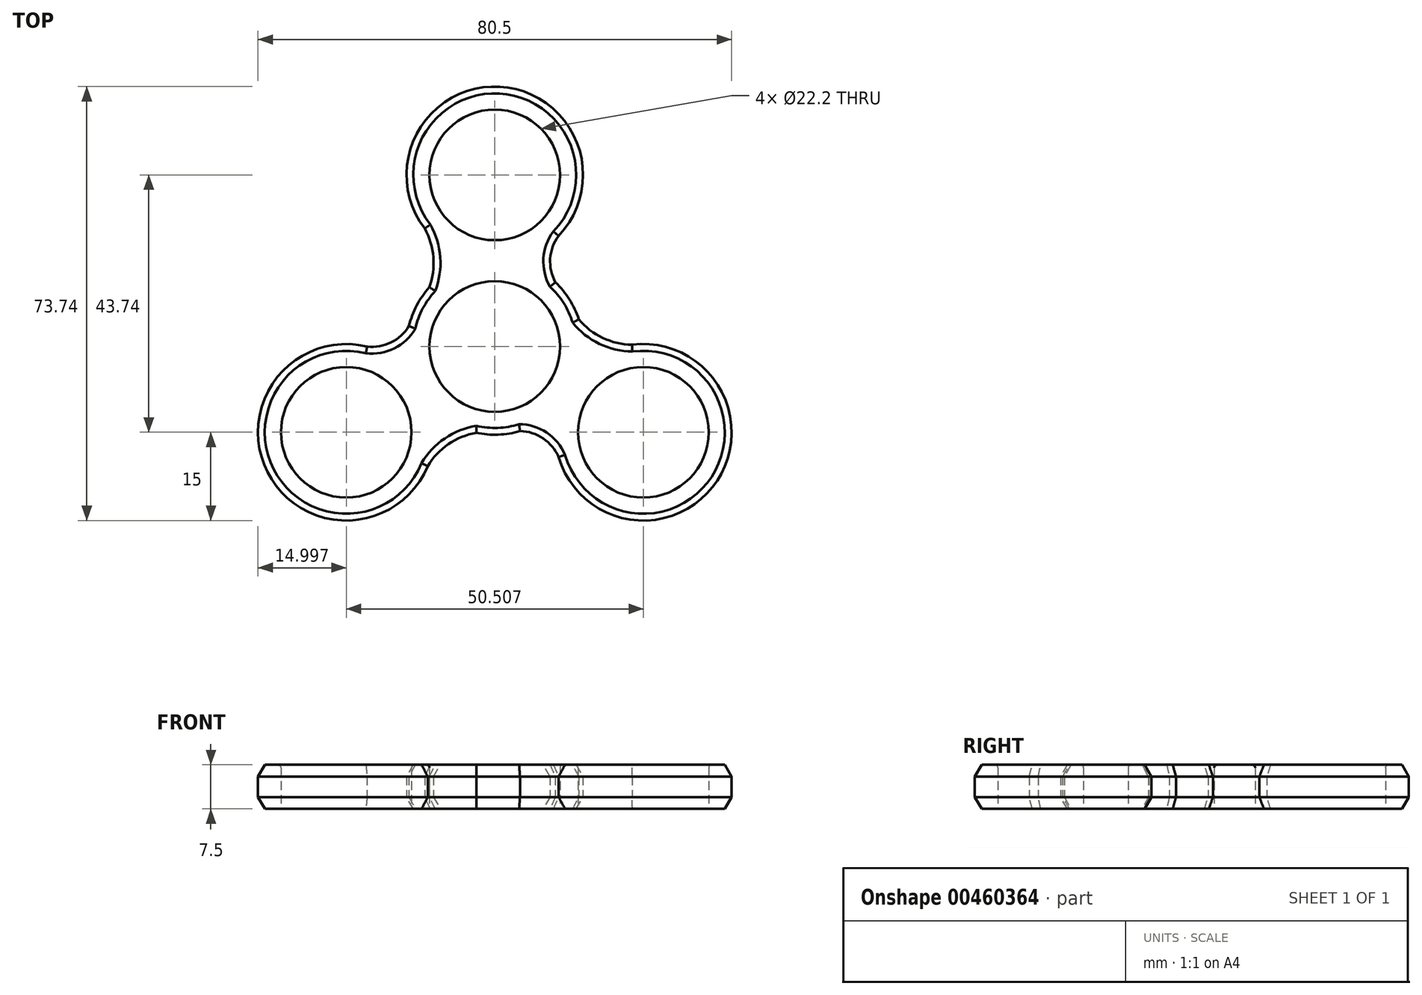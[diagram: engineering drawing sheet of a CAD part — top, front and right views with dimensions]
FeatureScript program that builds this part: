
annotation { "Feature Type Name" : "Feature", "Feature Type Description" : "" }
export const myFeature = defineFeature(function(context is Context, id is Id, definition is map)
    precondition{}
    {
        {
            var Q0;
            Q0=qCreatedBy(makeId("Top.planeOp"),FACE);
            var sketch = newSketch(context, id + "F0", { "sketchPlane" : qUnion([Q0])});
            skCircle(sketch, "E0", {"center": v(0, 0) * mm, "radius": 11.1 * mm});
            skCircle(sketch, "E1", {"center": v(0, 0) * mm, "radius": 15 * mm});
            skCircle(sketch, "E2", {"center": v(0, 29.16) * mm, "radius": 11.1 * mm});
            skCircle(sketch, "E3", {"center": v(0, 29.16) * mm, "radius": 15 * mm});
            skArc(sketch, "E4", {"start": v(-11.13, 10.06) * mm, "mid": v(-10.43, 15.14) * mm, "end": v(-11.92, 20.05) * mm});
            skArc(sketch, "E5", {"start": v(10.85, 18.8) * mm, "mid": v(9.41, 14.93) * mm, "end": v(10.3, 10.9) * mm});
            skCircle(sketch, "E6.1.0", {"center": v(-25.25, -14.58) * mm, "radius": 15 * mm});
            skCircle(sketch, "E6.1.1", {"center": v(-25.25, -14.58) * mm, "radius": 11.1 * mm});
            skArc(sketch, "E6.1.2", {"start": v(-3.15, -14.67) * mm, "mid": v(-7.9, -16.6) * mm, "end": v(-11.4, -20.35) * mm});
            skArc(sketch, "E6.1.3", {"start": v(-21.7, 0) * mm, "mid": v(-17.64, 0.69) * mm, "end": v(-14.6, 3.47) * mm});
            skCircle(sketch, "E6.2.0", {"center": v(25.25, -14.58) * mm, "radius": 15 * mm});
            skCircle(sketch, "E6.2.1", {"center": v(25.25, -14.58) * mm, "radius": 11.1 * mm});
            skArc(sketch, "E6.2.2", {"start": v(14.27, 4.6) * mm, "mid": v(18.33, 1.47) * mm, "end": v(23.33, 0.3) * mm});
            skArc(sketch, "E6.2.3", {"start": v(10.86, -18.8) * mm, "mid": v(8.22, -15.62) * mm, "end": v(4.29, -14.37) * mm});
            skSolve(sketch);
        }
        {
            var Q0;
            Q0=qSketchRegion(id+"F0",true);
            extrude(context, id + "F1", {"entities" : qUnion([Q0]), "depth" : 7.5 * mm, "offsetDistance" : 25 * mm});
        }
        {
            var Q0;
            {var subQ0=sQuery(id+"F0.wireOp",EDGE,"E6.2.0");var subQ1=sQuery(id+"F0.wireOp",EDGE,"E1");var subQ2=makeQuery(id+"F0.imprint","INTERSECT",VERTEX,{"disambiguationData":[OD(0.0)],"derivedFrom":[subQ1,subQ0]});Q0=makeQuery(id+"F0.imprint","IMPRINT",FACE,{"disambiguationData":[TD([[makeQuery(id+"F0.imprint","IMPRINT",EDGE,{"disambiguationData":[TD([[subQ2,-1.0]])],"derivedFrom":subQ1}),1.0]])]});}
            var Q1;
            {var subQ0=sQuery(id+"F0.wireOp",EDGE,"E6.1.0");var subQ1=sQuery(id+"F0.wireOp",EDGE,"E1");var subQ2=makeQuery(id+"F0.imprint","INTERSECT",VERTEX,{"disambiguationData":[OD(0.0)],"derivedFrom":[subQ1,subQ0]});Q1=makeQuery(id+"F0.imprint","IMPRINT",FACE,{"disambiguationData":[TD([[makeQuery(id+"F0.imprint","IMPRINT",EDGE,{"disambiguationData":[TD([[subQ2,-1.0]])],"derivedFrom":subQ1}),1.0]])]});}
            var Q2;
            {var subQ0=sQuery(id+"F0.wireOp",EDGE,"E3");var subQ1=sQuery(id+"F0.wireOp",EDGE,"E1");var subQ2=makeQuery(id+"F0.imprint","INTERSECT",VERTEX,{"disambiguationData":[OD(0.0)],"derivedFrom":[subQ1,subQ0]});Q2=makeQuery(id+"F0.imprint","IMPRINT",FACE,{"disambiguationData":[TD([[makeQuery(id+"F0.imprint","IMPRINT",EDGE,{"disambiguationData":[TD([[subQ2,-1.0]])],"derivedFrom":subQ1}),1.0]])]});}
            extrude(context, id + "F2", {"entities" : qUnion([Q0, Q1, Q2]), "operationType" : NewBodyOperationType.ADD, "depth" : 7.5 * mm, "offsetDistance" : 25 * mm});
        }
        {
            var Q0;
            Q0=makeQuery(id+"F1.opExtrude","CAP_EDGE",EDGE,{"disambiguationData":[OSD([sQuery(id+"F0.wireOp",EDGE,"E2")])],"isStart":false});
            var Q1;
            Q1=makeQuery(id+"F1.opExtrude","CAP_EDGE",EDGE,{"disambiguationData":[OSD([sQuery(id+"F0.wireOp",EDGE,"E0")])],"isStart":false});
            var Q2;
            Q2=makeQuery(id+"F1.opExtrude","CAP_EDGE",EDGE,{"disambiguationData":[OSD([sQuery(id+"F0.wireOp",EDGE,"E6.2.1")])],"isStart":false});
            var Q3;
            Q3=makeQuery(id+"F1.opExtrude","CAP_EDGE",EDGE,{"disambiguationData":[OSD([sQuery(id+"F0.wireOp",EDGE,"E6.1.1")])],"isStart":false});
            fillet(context, id + "F3", {"entities" : qUnion([Q0, Q1, Q2, Q3]), "radius" : 0.5 * mm, "tangentPropagation" : true, "allowEdgeOverflow" : false});
        }
        {
            var Q0;
            {var subQ0=sQuery(id+"F0.wireOp",EDGE,"E6.1.0");Q0=makeQuery(id+"F1.opExtrude","CAP_EDGE",EDGE,{"disambiguationData":[OSD([subQ0]),TDD([makeQuery(id+"F0.imprint","IMPRINT",EDGE,{"disambiguationData":[TD([[makeQuery(id+"F0.imprint","INTERSECT",VERTEX,{"derivedFrom":[subQ0,sQuery(id+"F0.wireOp",EDGE,"E6.1.2")]}),1.0]])],"derivedFrom":subQ0})])],"isStart":true});}
            var Q1;
            Q1=makeQuery(id+"F1.opExtrude","CAP_EDGE",EDGE,{"disambiguationData":[OSD([sQuery(id+"F0.wireOp",EDGE,"E6.1.3")])],"isStart":true});
            var Q2;
            Q2=makeQuery(id+"F1.opExtrude","CAP_EDGE",EDGE,{"disambiguationData":[OSD([sQuery(id+"F0.wireOp",EDGE,"E6.1.2")])],"isStart":true});
            var Q3;
            Q3=makeQuery(id+"F1.opExtrude","CAP_EDGE",EDGE,{"disambiguationData":[OSD([sQuery(id+"F0.wireOp",EDGE,"E6.2.3")])],"isStart":true});
            var Q4;
            {var subQ0=sQuery(id+"F0.wireOp",EDGE,"E6.2.0");Q4=makeQuery(id+"F1.opExtrude","CAP_EDGE",EDGE,{"disambiguationData":[OSD([subQ0]),TDD([makeQuery(id+"F0.imprint","IMPRINT",EDGE,{"disambiguationData":[TD([[makeQuery(id+"F0.imprint","INTERSECT",VERTEX,{"derivedFrom":[subQ0,sQuery(id+"F0.wireOp",EDGE,"E6.2.2")]}),1.0]])],"derivedFrom":subQ0})])],"isStart":true});}
            var Q5;
            Q5=makeQuery(id+"F1.opExtrude","CAP_EDGE",EDGE,{"disambiguationData":[OSD([sQuery(id+"F0.wireOp",EDGE,"E6.2.2")])],"isStart":true});
            var Q6;
            Q6=makeQuery(id+"F1.opExtrude","CAP_EDGE",EDGE,{"disambiguationData":[OSD([sQuery(id+"F0.wireOp",EDGE,"E5")])],"isStart":true});
            var Q7;
            {var subQ0=sQuery(id+"F0.wireOp",EDGE,"E3");Q7=makeQuery(id+"F1.opExtrude","CAP_EDGE",EDGE,{"disambiguationData":[OSD([subQ0]),TDD([makeQuery(id+"F0.imprint","IMPRINT",EDGE,{"disambiguationData":[TD([[makeQuery(id+"F0.imprint","INTERSECT",VERTEX,{"derivedFrom":[subQ0,sQuery(id+"F0.wireOp",EDGE,"E4")]}),1.0]])],"derivedFrom":subQ0})])],"isStart":true});}
            var Q8;
            Q8=makeQuery(id+"F1.opExtrude","CAP_EDGE",EDGE,{"disambiguationData":[OSD([sQuery(id+"F0.wireOp",EDGE,"E4")])],"isStart":true});
            var Q9;
            {var subQ0=sQuery(id+"F0.wireOp",EDGE,"E1");Q9=makeQuery(id+"F1.opExtrude","CAP_EDGE",EDGE,{"disambiguationData":[OSD([subQ0]),TDD([makeQuery(id+"F0.imprint","IMPRINT",EDGE,{"disambiguationData":[TD([[makeQuery(id+"F0.imprint","INTERSECT",VERTEX,{"derivedFrom":[subQ0,sQuery(id+"F0.wireOp",EDGE,"E5")]}),1.0]])],"derivedFrom":subQ0})])],"isStart":true});}
            var Q10;
            {var subQ0=sQuery(id+"F0.wireOp",EDGE,"E1");Q10=makeQuery(id+"F1.opExtrude","CAP_EDGE",EDGE,{"disambiguationData":[OSD([subQ0]),TDD([makeQuery(id+"F0.imprint","IMPRINT",EDGE,{"disambiguationData":[TD([[makeQuery(id+"F0.imprint","INTERSECT",VERTEX,{"derivedFrom":[subQ0,sQuery(id+"F0.wireOp",EDGE,"E4")]}),-1.0]])],"derivedFrom":subQ0})])],"isStart":true});}
            var Q11;
            {var subQ0=sQuery(id+"F0.wireOp",EDGE,"E1");Q11=makeQuery(id+"F1.opExtrude","CAP_EDGE",EDGE,{"disambiguationData":[OSD([subQ0]),TDD([makeQuery(id+"F0.imprint","IMPRINT",EDGE,{"disambiguationData":[TD([[makeQuery(id+"F0.imprint","INTERSECT",VERTEX,{"derivedFrom":[subQ0,sQuery(id+"F0.wireOp",EDGE,"E6.1.2")]}),-1.0]])],"derivedFrom":subQ0})])],"isStart":true});}
            chamfer(context, id + "F4", {"entities" : qUnion([Q0, Q1, Q2, Q3, Q4, Q5, Q6, Q7, Q8, Q9, Q10, Q11]), "chamferType" : ChamferType.OFFSET_ANGLE, "width" : 2 * mm, "oppositeDirection" : false, "angle" : 30 * degree, "tangentPropagation" : true});
        }
        {
            var Q0;
            {var subQ0=sQuery(id+"F0.wireOp",EDGE,"E6.1.0");Q0=makeQuery(id+"F1.opExtrude","CAP_EDGE",EDGE,{"disambiguationData":[OSD([subQ0]),TDD([makeQuery(id+"F0.imprint","IMPRINT",EDGE,{"disambiguationData":[TD([[makeQuery(id+"F0.imprint","INTERSECT",VERTEX,{"derivedFrom":[subQ0,sQuery(id+"F0.wireOp",EDGE,"E6.1.2")]}),1.0]])],"derivedFrom":subQ0})])],"isStart":false});}
            var Q1;
            Q1=makeQuery(id+"F1.opExtrude","CAP_EDGE",EDGE,{"disambiguationData":[OSD([sQuery(id+"F0.wireOp",EDGE,"E6.1.2")])],"isStart":false});
            var Q2;
            Q2=makeQuery(id+"F1.opExtrude","CAP_EDGE",EDGE,{"disambiguationData":[OSD([sQuery(id+"F0.wireOp",EDGE,"E6.1.3")])],"isStart":false});
            var Q3;
            Q3=makeQuery(id+"F1.opExtrude","CAP_EDGE",EDGE,{"disambiguationData":[OSD([sQuery(id+"F0.wireOp",EDGE,"E6.2.3")])],"isStart":false});
            var Q4;
            {var subQ0=sQuery(id+"F0.wireOp",EDGE,"E6.2.0");Q4=makeQuery(id+"F1.opExtrude","CAP_EDGE",EDGE,{"disambiguationData":[OSD([subQ0]),TDD([makeQuery(id+"F0.imprint","IMPRINT",EDGE,{"disambiguationData":[TD([[makeQuery(id+"F0.imprint","INTERSECT",VERTEX,{"derivedFrom":[subQ0,sQuery(id+"F0.wireOp",EDGE,"E6.2.2")]}),1.0]])],"derivedFrom":subQ0})])],"isStart":false});}
            var Q5;
            Q5=makeQuery(id+"F1.opExtrude","CAP_EDGE",EDGE,{"disambiguationData":[OSD([sQuery(id+"F0.wireOp",EDGE,"E4")])],"isStart":false});
            var Q6;
            {var subQ0=sQuery(id+"F0.wireOp",EDGE,"E3");Q6=makeQuery(id+"F1.opExtrude","CAP_EDGE",EDGE,{"disambiguationData":[OSD([subQ0]),TDD([makeQuery(id+"F0.imprint","IMPRINT",EDGE,{"disambiguationData":[TD([[makeQuery(id+"F0.imprint","INTERSECT",VERTEX,{"derivedFrom":[subQ0,sQuery(id+"F0.wireOp",EDGE,"E4")]}),1.0]])],"derivedFrom":subQ0})])],"isStart":false});}
            var Q7;
            Q7=makeQuery(id+"F1.opExtrude","CAP_EDGE",EDGE,{"disambiguationData":[OSD([sQuery(id+"F0.wireOp",EDGE,"E5")])],"isStart":false});
            var Q8;
            Q8=makeQuery(id+"F1.opExtrude","CAP_EDGE",EDGE,{"disambiguationData":[OSD([sQuery(id+"F0.wireOp",EDGE,"E6.2.2")])],"isStart":false});
            var Q9;
            {var subQ0=sQuery(id+"F0.wireOp",EDGE,"E1");Q9=makeQuery(id+"F1.opExtrude","CAP_EDGE",EDGE,{"disambiguationData":[OSD([subQ0]),TDD([makeQuery(id+"F0.imprint","IMPRINT",EDGE,{"disambiguationData":[TD([[makeQuery(id+"F0.imprint","INTERSECT",VERTEX,{"derivedFrom":[subQ0,sQuery(id+"F0.wireOp",EDGE,"E5")]}),1.0]])],"derivedFrom":subQ0})])],"isStart":false});}
            var Q10;
            {var subQ0=sQuery(id+"F0.wireOp",EDGE,"E1");Q10=makeQuery(id+"F1.opExtrude","CAP_EDGE",EDGE,{"disambiguationData":[OSD([subQ0]),TDD([makeQuery(id+"F0.imprint","IMPRINT",EDGE,{"disambiguationData":[TD([[makeQuery(id+"F0.imprint","INTERSECT",VERTEX,{"derivedFrom":[subQ0,sQuery(id+"F0.wireOp",EDGE,"E4")]}),-1.0]])],"derivedFrom":subQ0})])],"isStart":false});}
            var Q11;
            {var subQ0=sQuery(id+"F0.wireOp",EDGE,"E1");Q11=makeQuery(id+"F1.opExtrude","CAP_EDGE",EDGE,{"disambiguationData":[OSD([subQ0]),TDD([makeQuery(id+"F0.imprint","IMPRINT",EDGE,{"disambiguationData":[TD([[makeQuery(id+"F0.imprint","INTERSECT",VERTEX,{"derivedFrom":[subQ0,sQuery(id+"F0.wireOp",EDGE,"E6.1.2")]}),-1.0]])],"derivedFrom":subQ0})])],"isStart":false});}
            chamfer(context, id + "F5", {"entities" : qUnion([Q0, Q1, Q2, Q3, Q4, Q5, Q6, Q7, Q8, Q9, Q10, Q11]), "chamferType" : ChamferType.OFFSET_ANGLE, "width" : 2 * mm, "oppositeDirection" : true, "angle" : 30 * degree, "tangentPropagation" : true});
        }
    });
